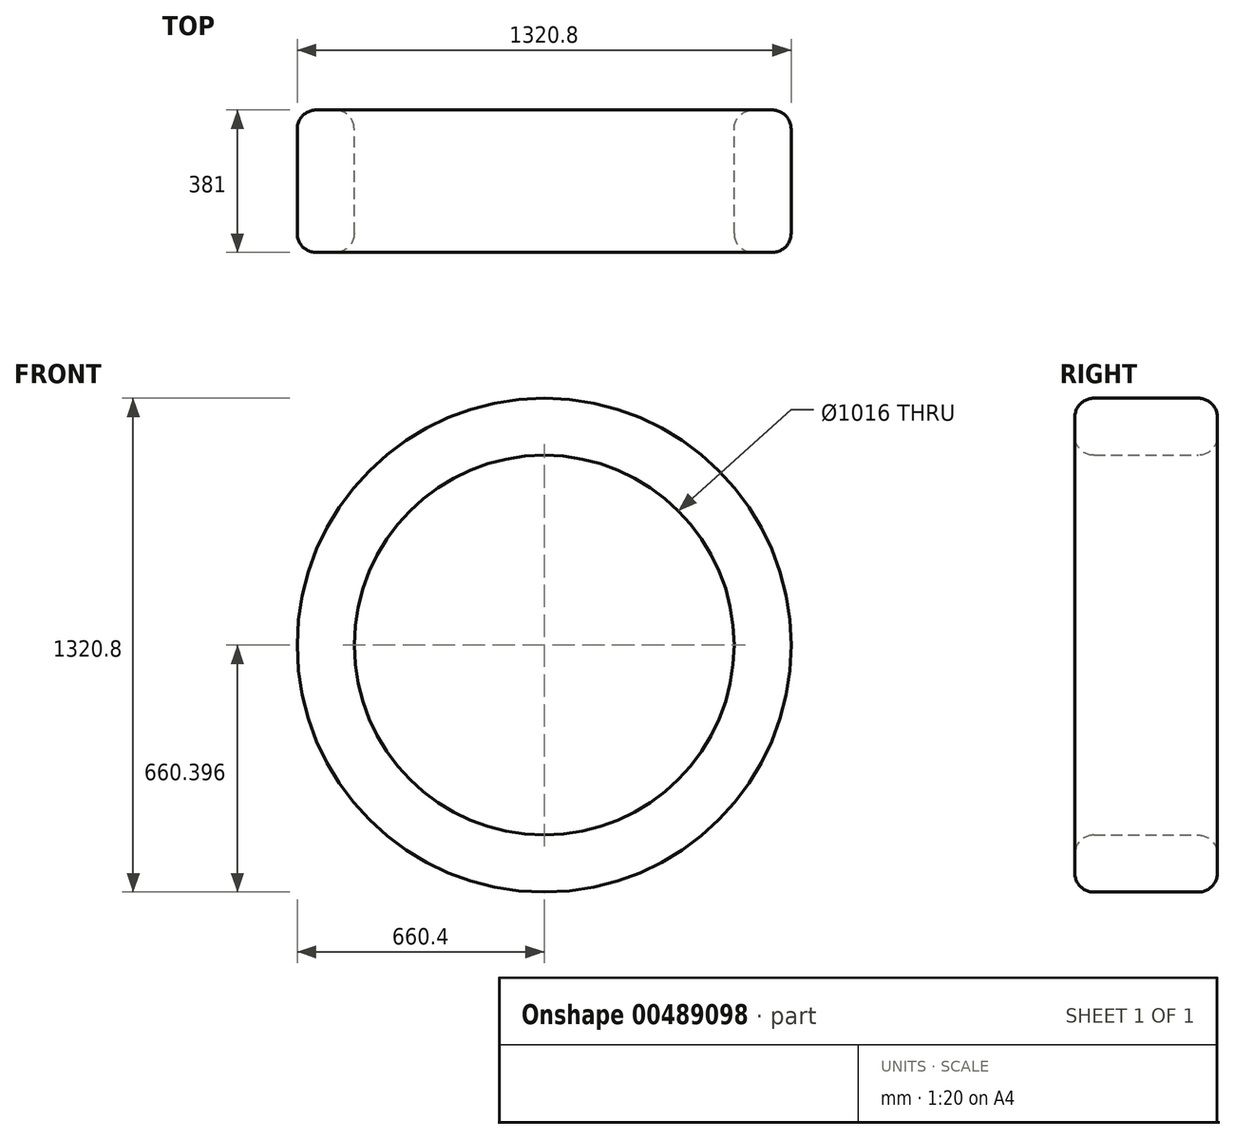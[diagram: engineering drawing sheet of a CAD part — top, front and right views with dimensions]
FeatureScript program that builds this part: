
annotation { "Feature Type Name" : "Feature", "Feature Type Description" : "" }
export const myFeature = defineFeature(function(context is Context, id is Id, definition is map)
    precondition{}
    {
        {
            var Q0;
            Q0=qCreatedBy(makeId("Right.planeOp"),FACE);
            var sketch = newSketch(context, id + "F0", { "sketchPlane" : qUnion([Q0])});
            skLineSegment(sketch, "E0.bottom", {"start": v(138.95, 70.75) * mm, "end": v(-140.45, 70.75) * mm});
            skLineSegment(sketch, "E0.top", {"start": v(138.95, -81.65) * mm, "end": v(-140.45, -81.65) * mm});
            skLineSegment(sketch, "E0.left", {"start": v(189.75, 19.95) * mm, "end": v(189.75, -30.85) * mm});
            skLineSegment(sketch, "E0.right", {"start": v(-191.25, 19.95) * mm, "end": v(-191.25, -30.85) * mm});
            skPoint(sketch, "E1.visualSharp", {"position": v(189.75, 70.75) * mm});
            skArc(sketch, "E1.filletArc", {"start": v(189.75, 19.95) * mm, "mid": v(174.87, 55.87) * mm, "end": v(138.95, 70.75) * mm});
            skPoint(sketch, "E2.visualSharp", {"position": v(189.75, -81.65) * mm});
            skArc(sketch, "E2.filletArc", {"start": v(138.95, -81.65) * mm, "mid": v(174.87, -66.78) * mm, "end": v(189.75, -30.85) * mm});
            skPoint(sketch, "E3.visualSharp", {"position": v(-191.25, -81.65) * mm});
            skArc(sketch, "E3.filletArc", {"start": v(-191.25, -30.85) * mm, "mid": v(-176.37, -66.78) * mm, "end": v(-140.45, -81.65) * mm});
            skPoint(sketch, "E4.visualSharp", {"position": v(-191.25, 70.75) * mm});
            skArc(sketch, "E4.filletArc", {"start": v(-140.45, 70.75) * mm, "mid": v(-176.37, 55.87) * mm, "end": v(-191.25, 19.95) * mm});
            skLineSegment(sketch, "E5", {"start": v(138.95, -589.65) * mm, "end": v(-140.45, -589.65) * mm});
            skSolve(sketch);
        }
        {
            var Q0;
            Q0 = qSketchRegion(id + "F0", true);
            var Q1;
            Q1=sQuery(id+"F0.wireOp",EDGE,"E5");
            revolve(context, id + "F1", {"entities" : qUnion([Q0]), "axis" : qUnion([Q1]), "revolveType" : RevolveType.FULL});
        }
    });
